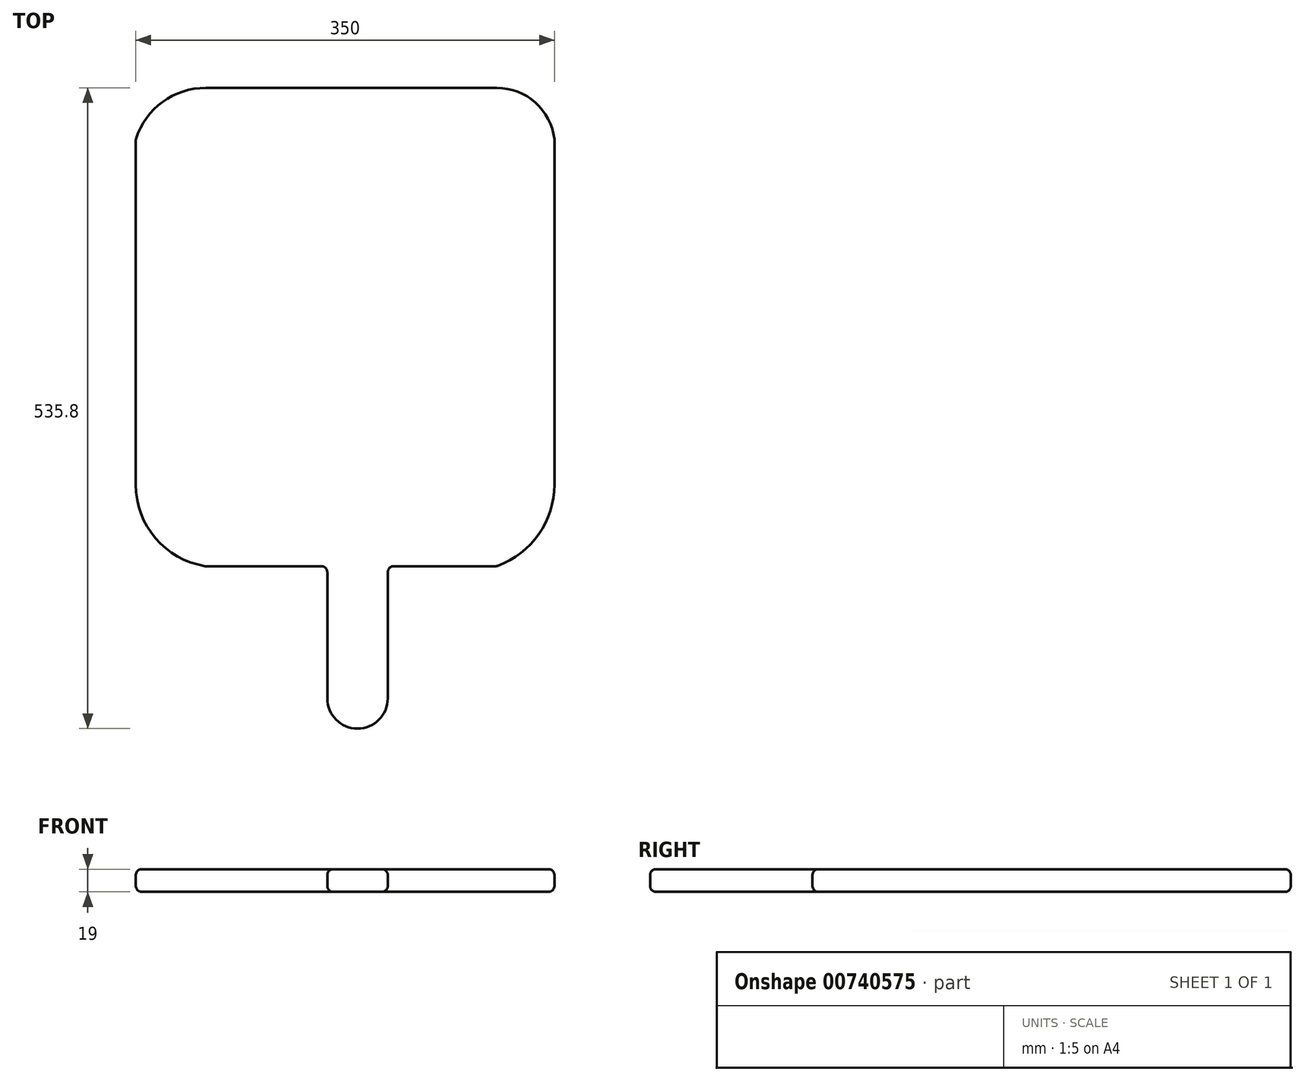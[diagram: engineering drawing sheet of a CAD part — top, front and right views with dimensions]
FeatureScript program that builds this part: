
annotation { "Feature Type Name" : "Feature", "Feature Type Description" : "" }
export const myFeature = defineFeature(function(context is Context, id is Id, definition is map)
    precondition{}
    {
        {
            var Q0;
            Q0=qCreatedBy(makeId("Top.planeOp"),FACE);
            var sketch = newSketch(context, id + "F0", { "sketchPlane" : qUnion([Q0])});
            skLineSegment(sketch, "E0", {"start": v(-101.57, 265.06) * mm, "end": v(141.7, 265.06) * mm});
            skArc(sketch, "E1", {"start": v(189.9, 221.74) * mm, "mid": v(174.1, 252.64) * mm, "end": v(141.7, 265.06) * mm});
            skLineSegment(sketch, "E2", {"start": v(189.9, 221.74) * mm, "end": v(189.9, -66.77) * mm});
            skArc(sketch, "E3", {"start": v(-101.57, 265.06) * mm, "mid": v(-137.98, 253.05) * mm, "end": v(-160.1, 221.74) * mm});
            skLineSegment(sketch, "E4", {"start": v(-160.1, 221.74) * mm, "end": v(-160.1, -66.77) * mm});
            skArc(sketch, "E5", {"start": v(-160.1, -66.77) * mm, "mid": v(-143.46, -111.7) * mm, "end": v(-101.57, -134.94) * mm});
            skLineSegment(sketch, "E6", {"start": v(-101.57, -134.94) * mm, "end": v(0, -134.94) * mm});
            skLineSegment(sketch, "E7", {"start": v(141.4, -134.94) * mm, "end": v(50.57, -134.94) * mm});
            skLineSegment(sketch, "E8", {"start": v(50.57, -134.94) * mm, "end": v(50.57, -245.45) * mm});
            skArc(sketch, "E9", {"start": v(0, -245.45) * mm, "mid": v(25.29, -270.74) * mm, "end": v(50.57, -245.45) * mm});
            skLineSegment(sketch, "E10", {"start": v(0, -134.94) * mm, "end": v(0, -245.45) * mm});
            skArc(sketch, "E11", {"start": v(141.4, -134.94) * mm, "mid": v(176.54, -108.6) * mm, "end": v(189.9, -66.77) * mm});
            skSolve(sketch);
        }
        {
            var Q0;
            Q0 = qSketchRegion(id + "F0", true);
            extrude(context, id + "F1", {"entities" : qUnion([Q0]), "depth" : 19 * mm, "offsetDistance" : 25.4 * mm});
        }
        {
            var Q0;
            Q0=makeQuery(id+"F1.opExtrude","SWEPT_FACE",FACE,{"disambiguationData":[OSD([sQuery(id+"F0.wireOp",EDGE,"E4")])]});
            var Q1;
            Q1=makeQuery(id+"F1.opExtrude","SWEPT_FACE",FACE,{"disambiguationData":[OSD([sQuery(id+"F0.wireOp",EDGE,"E5")])]});
            var Q2;
            Q2=makeQuery(id+"F1.opExtrude","CAP_EDGE",EDGE,{"disambiguationData":[OSD([sQuery(id+"F0.wireOp",EDGE,"E6")])],"isStart":false});
            var Q3;
            Q3=makeQuery(id+"F1.opExtrude","CAP_EDGE",EDGE,{"disambiguationData":[OSD([sQuery(id+"F0.wireOp",EDGE,"E6")])],"isStart":true});
            var Q4;
            Q4=makeQuery(id+"F1.opExtrude","SWEPT_FACE",FACE,{"disambiguationData":[OSD([sQuery(id+"F0.wireOp",EDGE,"E10")])]});
            var Q5;
            Q5=makeQuery(id+"F1.opExtrude","SWEPT_FACE",FACE,{"disambiguationData":[OSD([sQuery(id+"F0.wireOp",EDGE,"E7")])]});
            var Q6;
            Q6=makeQuery(id+"F1.opExtrude","SWEPT_FACE",FACE,{"disambiguationData":[OSD([sQuery(id+"F0.wireOp",EDGE,"E11")])]});
            var Q7;
            Q7=makeQuery(id+"F1.opExtrude","SWEPT_FACE",FACE,{"disambiguationData":[OSD([sQuery(id+"F0.wireOp",EDGE,"E1")])]});
            fillet(context, id + "F2", {"entities" : qUnion([Q0, Q1, Q2, Q3, Q4, Q5, Q6, Q7]), "radius" : 5 * mm, "tangentPropagation" : true, "allowEdgeOverflow" : false});
        }
    });
